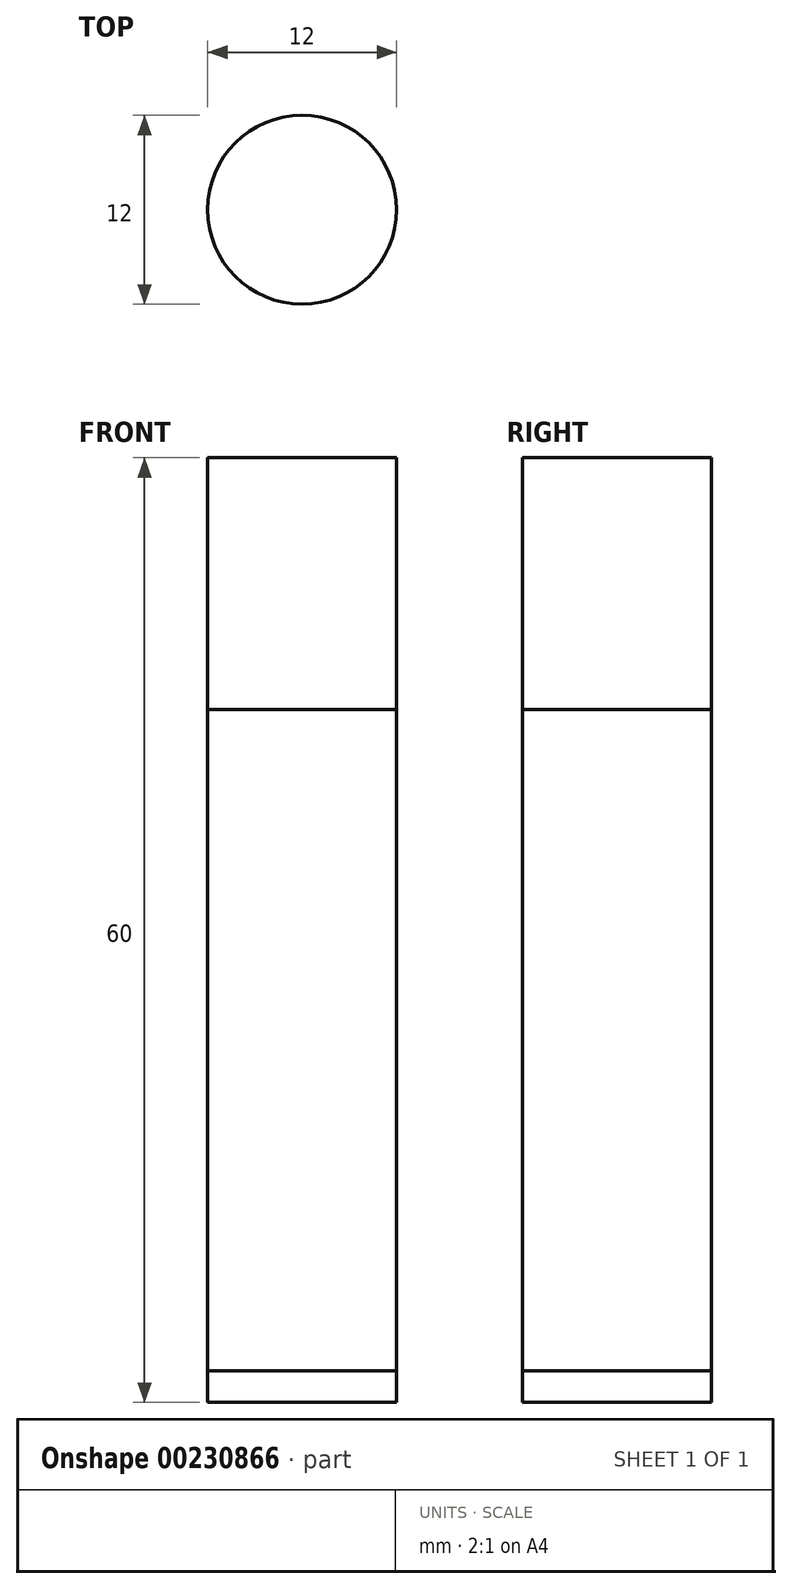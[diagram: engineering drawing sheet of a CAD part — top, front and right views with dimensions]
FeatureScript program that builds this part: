
annotation { "Feature Type Name" : "Feature", "Feature Type Description" : "" }
export const myFeature = defineFeature(function(context is Context, id is Id, definition is map)
    precondition{}
    {
        {
            var Q0;
            Q0=qCreatedBy(makeId("Top.planeOp"),FACE);
            var sketch = newSketch(context, id + "F0", { "sketchPlane" : qUnion([Q0])});
            skCircle(sketch, "E0", {"center": v(0, 0) * mm, "radius": 6 * mm});
            skSolve(sketch);
        }
        {
            var Q0;
            Q0 = qSketchRegion(id + "F0", true);
            extrude(context, id + "F1", {"entities" : qUnion([Q0]), "depth" : 2 * mm});
        }
        {
            var Q0;
            Q0=makeQuery(id+"F1.opExtrude","CAP_FACE",FACE,{"disambiguationData":[OSD([sQuery(id+"F0.wireOp",EDGE,"E0")])],"isStart":false});
            var sketch = newSketch(context, id + "F2", { "sketchPlane" : qUnion([Q0])});
            skCircle(sketch, "E1.0", {"center": v(0, 0) * mm, "radius": 6 * mm});
            skSolve(sketch);
        }
        {
            var Q0;
            Q0 = qSketchRegion(id + "F2", true);
            extrude(context, id + "F3", {"entities" : qUnion([Q0]), "depth" : 42 * mm});
        }
        {
            var Q0;
            Q0=makeQuery(id+"F3.opExtrude","CAP_FACE",FACE,{"disambiguationData":[OSD([sQuery(id+"F2.wireOp",EDGE,"E1.0")])],"isStart":false});
            var sketch = newSketch(context, id + "F4", { "sketchPlane" : qUnion([Q0])});
            skCircle(sketch, "E2.0", {"center": v(0, 0) * mm, "radius": 6 * mm});
            skSolve(sketch);
        }
        {
            var Q0;
            Q0 = qSketchRegion(id + "F4", true);
            extrude(context, id + "F5", {"entities" : qUnion([Q0]), "depth" : 16 * mm});
        }
    });
